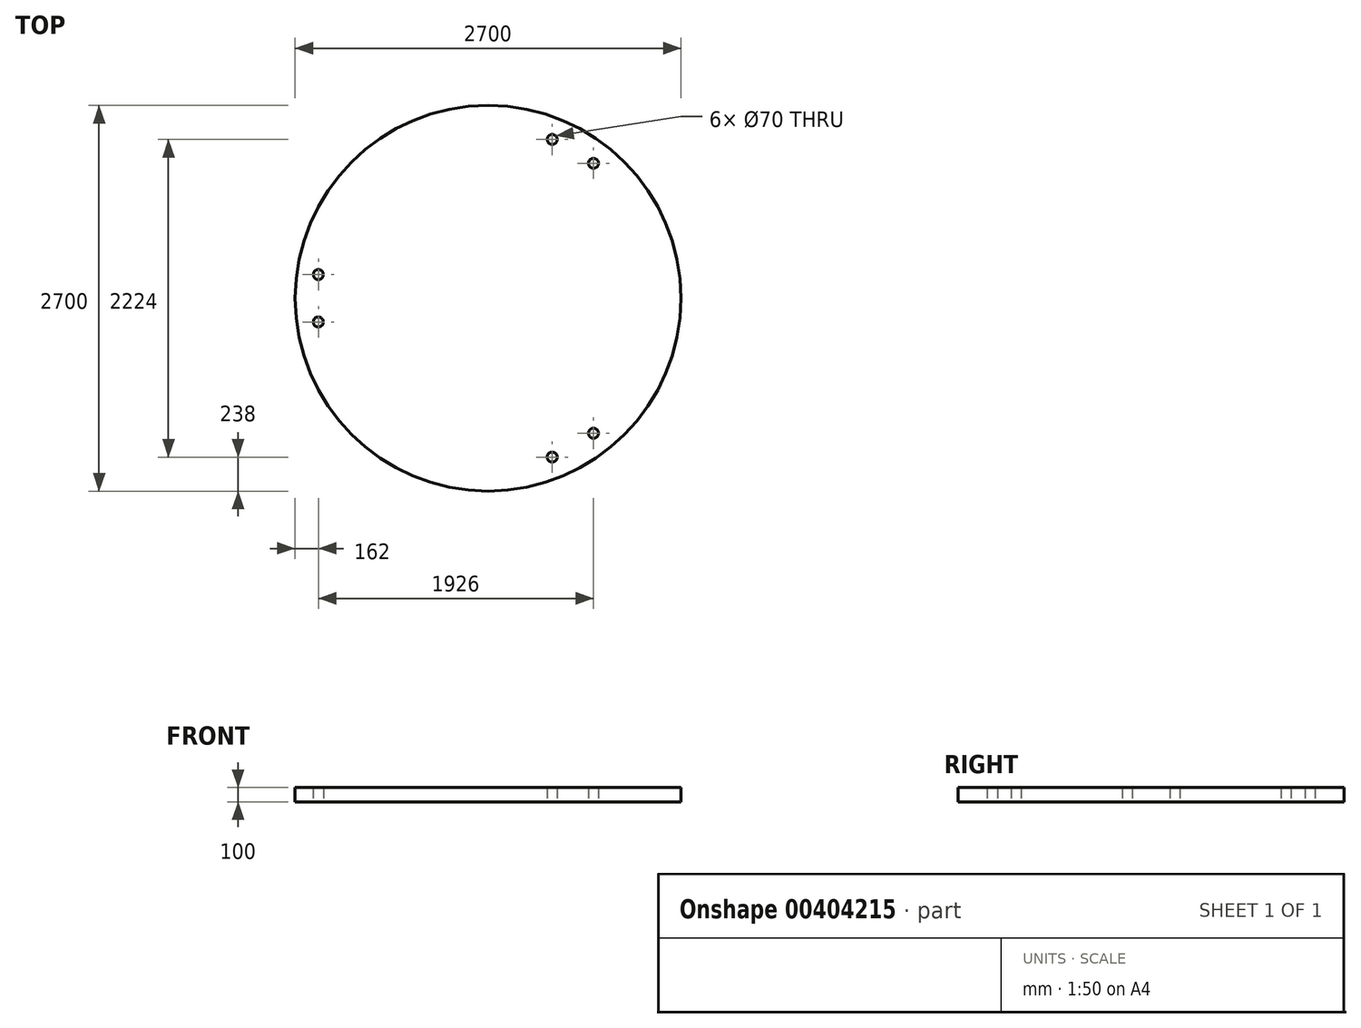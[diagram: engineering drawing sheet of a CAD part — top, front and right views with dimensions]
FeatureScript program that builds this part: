
annotation { "Feature Type Name" : "Feature", "Feature Type Description" : "" }
export const myFeature = defineFeature(function(context is Context, id is Id, definition is map)
    precondition{}
    {
        {
            var Q0;
            Q0=qCreatedBy(makeId("Top.planeOp"),FACE);
            var sketch = newSketch(context, id + "F0", { "sketchPlane" : qUnion([Q0])});
            skCircle(sketch, "E0", {"center": v(-1188, -166) * mm, "radius": 35 * mm});
            skCircle(sketch, "E1", {"center": v(-1188, 166) * mm, "radius": 35 * mm});
            skCircle(sketch, "E2", {"center": v(449, 1112) * mm, "radius": 35 * mm});
            skCircle(sketch, "E3", {"center": v(449, -1112) * mm, "radius": 35 * mm});
            skCircle(sketch, "E4", {"center": v(738, 945) * mm, "radius": 35 * mm});
            skCircle(sketch, "E5", {"center": v(738, -945) * mm, "radius": 35 * mm});
            skCircle(sketch, "E6", {"center": v(0, 0) * mm, "radius": 1350 * mm});
            skSolve(sketch);
        }
        {
            var Q0;
            Q0=makeQuery(id+"F0.imprint","IMPRINT",FACE,{"disambiguationData":[TD([[makeQuery(id+"F0.imprint","IMPRINT",EDGE,{"derivedFrom":sQuery(id+"F0.wireOp",EDGE,"E0")}),-1.0]])]});
            extrude(context, id + "F1", {"entities" : qUnion([Q0]), "depth" : 100 * mm});
        }
    });
